# Revit family: Vitra-Built-inBath&ShowerMixer(ConcealedPart)-SentoSeries-A42213
name_source: partatom
category: Plumbing Fixtures
units: mm (PartAtom-declared; Revit-internal decimal feet)

## family parameters
Always vertical = Yes
Cut with Voids When Loaded = No
Host = Wall
OmniClass Number = 23.45.55.17
OmniClass Title = Mixing Faucets
Part Type = Normal
Room Calculation Point = No
Round Connector Dimension = Use Diameter
Shared = Yes

## types (1)
- Built-inBath&ShowerMixer(ConcealedPart)-Vitra-SentoSeries-A42213
    Article No. (default) = A42213
    BIMobject category = Taps & Mixers
    CW Connection = Yes
    CWFU = 0
    Coating Material = Steel, Chrome Plated
    Connection Diameter (mm) = 10 mm  [stored 0.0328084 ft]
    Cost = 0 $
    Date of publishing = 2019
    Default Elevation = 800 mm  [stored 2.62467 ft]
    Depth (mm) = 138 mm  [stored 0.452756 ft]
    Design country = Turkey
    HW Connection = Yes
    HWFU = 0
    Height (mm) = 74 mm  [stored 0.242782 ft]
    Hot Water Supply (max.) = 90 °C
    Hot Water temperature, factory set to = 38 °C
    IFC Classification = Sanitary Terminal
    Main Material = Brass
    Manufacturer = Vitra
    Manufacturer name = Vitra
    Masterformat 2014 Code = 22 40 00
    Masterformat 2014 Description = Plumbing Fixtures
    Min. flow pressure of = 0.5 bar
    Model = A42213
    MountingType = Wall-mounted (Concealed Part)
    NBS Reference Code = 45-35-70/315
    NBS Reference Description = Water supply fittings for wash basins and troughs
    Nominal Height = 0 mm  [stored 0 ft]
    Nominal Length = 0 mm  [stored 0 ft]
    Nominal Width = 0 mm  [stored 0 ft]
    Number Of Connections = 3
    OmniClass Code = 23.45.55.17
    OmniClass Description = Mixing Faucets
    Product Guid = https://cdn.vitra.com.tr
    Product Properties = Extra Water Saving, Green Building Certification, Energy Saving, Easy İnstallation
    Product SKU = A42213
    Product Type = Built-in Bath/Shower Mixer (Concealed Part)
    Product certification = https://vitraglobal.com
    Product data url = https://vitraglobal.com
    Product family = Sento
    Product group = Sento Built-in Bath/Shower Mixer(Concealed Part)
    Range of Hot Water Supply = 5 - 65 °C
    Range of flow pressure = 1 - 5 bar
    Spares Availability Duration = 7 Years
    Technical description = https://vitraglobal.com
    Test Pressure = 16 bar
    UNSPSC Code = 301815
    URL = https://vitraglobal.com
    Uniclass 1.4 Code = L725111
    Uniclass 1.4 Description = Mixer taps
    Uniclass 2.0 Code = Pr_40_30_96_98
    Uniclass 2.0 Description = Washbasin Tap
    Uniclass 2015 Code = Pr_40_20_87_98
    Uniclass 2015 Name = Washbasin Tap
    Uniformat II Code = 22 40 00
    Uniformat II Description = Plumbing Fixture
    WFU = 0
    Weight Net (Kg) = 0,630
    Width (mm) = 80 mm  [stored 0.262467 ft]
    Youtube = https://www.youtube.com

note: [stored X ft] marks values corroborated as IEEE doubles in the binary element streams (Revit-internal decimal feet)

## geometry (parser evidence)
native form markers: Sweep x5
no freeform markers — native parametric forms only
